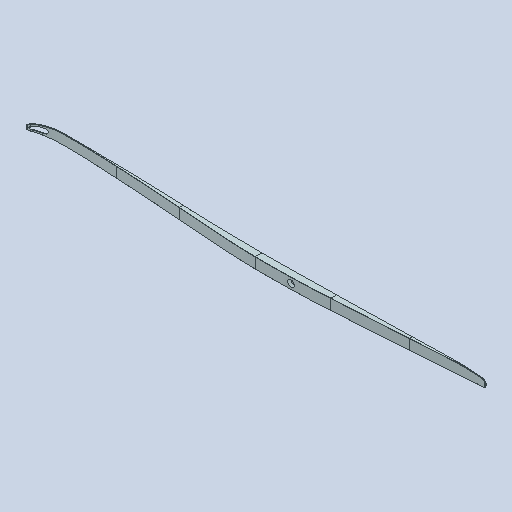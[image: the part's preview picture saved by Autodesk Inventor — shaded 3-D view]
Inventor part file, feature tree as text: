
AUTODESK INVENTOR PART (.ipt)
format: ipt  version: 2024 (Build 280153000, 153)  size: 808,960 bytes
history: native  units: in
note: dims shown in document units (in); Inventor stores cm internally (conversion verified against a paired STEP export)
features: other x1, sketch x1
ambient origin geometry x8: Origin, YZ Plane, XZ Plane, XY Plane, X Axis, Y Axis, Z Axis, Center Point
bodies: Solid1 (feature_tree), Solid2 (feature_tree)
feature tree (2):
  other  "Repaired Geometry1"
  sketch  "Sketch1"
